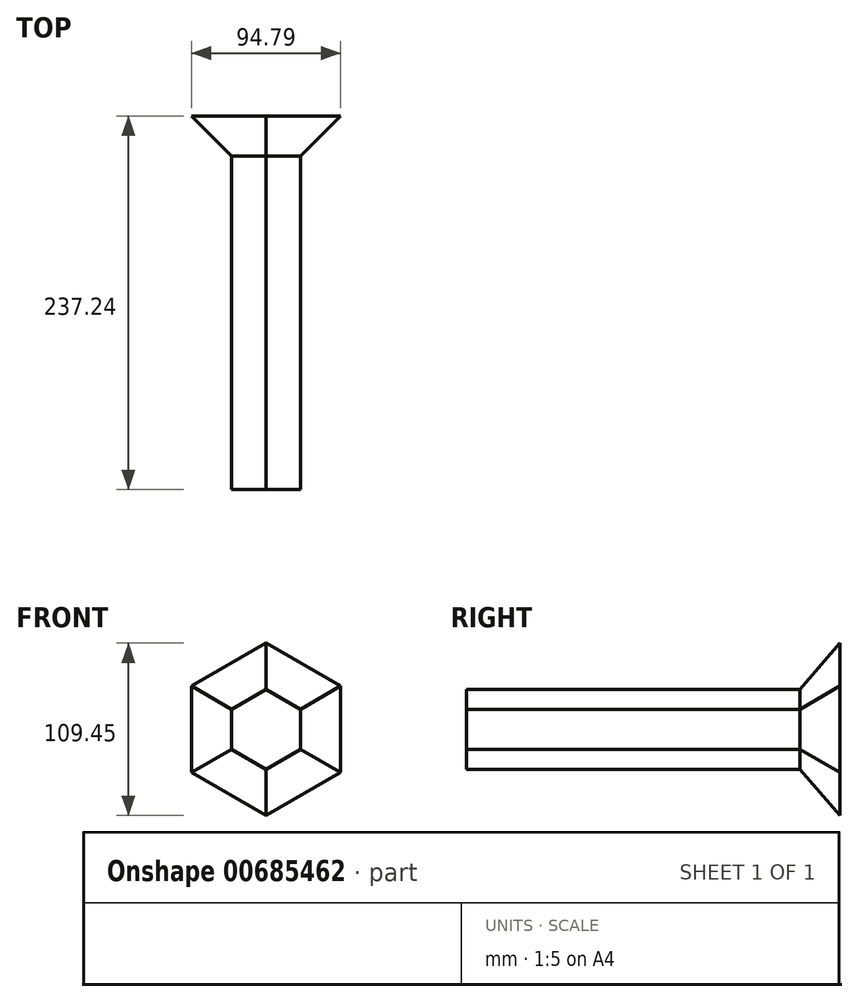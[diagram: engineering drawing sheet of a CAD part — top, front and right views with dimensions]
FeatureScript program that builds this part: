
annotation { "Feature Type Name" : "Feature", "Feature Type Description" : "" }
export const myFeature = defineFeature(function(context is Context, id is Id, definition is map)
    precondition{}
    {
        {
            var Q0;
            Q0=qCreatedBy(makeId("Front.planeOp"),FACE);
            var sketch = newSketch(context, id + "F0", { "sketchPlane" : qUnion([Q0])});
            skPoint(sketch, "E0.0.midPoint", {"position": v(16.7, -5.43) * mm});
            skLineSegment(sketch, "E1.0", {"start": v(19.21, 13.6) * mm, "end": v(19.21, -11.8) * mm});
            skLineSegment(sketch, "E1.1", {"start": v(19.21, -11.8) * mm, "end": v(-2.78, -24.5) * mm});
            skLineSegment(sketch, "E1.2", {"start": v(-2.78, -24.5) * mm, "end": v(-24.78, -11.8) * mm});
            skLineSegment(sketch, "E1.3", {"start": v(-24.78, -11.8) * mm, "end": v(-24.78, 13.6) * mm});
            skLineSegment(sketch, "E1.4", {"start": v(-24.78, 13.6) * mm, "end": v(-2.78, 26.3) * mm});
            skLineSegment(sketch, "E1.5", {"start": v(-2.78, 26.3) * mm, "end": v(19.21, 13.6) * mm});
            skSolve(sketch);
        }
        {
            var Q0;
            Q0=makeQuery(id+"F0.imprint","IMPRINT",FACE,{"disambiguationData":[TD([[makeQuery(id+"F0.imprint","IMPRINT",EDGE,{"derivedFrom":sQuery(id+"F0.wireOp",EDGE,"E1.0")}),-1.0]])]});
            extrude(context, id + "F1", {"entities" : qUnion([Q0]), "depth" : 211.84 * mm, "offsetDistance" : 25.4 * mm});
        }
        {
            var Q0;
            Q0=makeQuery(id+"F1.opExtrude","CAP_FACE",FACE,{"disambiguationData":[OSD([sQuery(id+"F0.wireOp",EDGE,"E1.0"),sQuery(id+"F0.wireOp",EDGE,"E1.1"),sQuery(id+"F0.wireOp",EDGE,"E1.2"),sQuery(id+"F0.wireOp",EDGE,"E1.3"),sQuery(id+"F0.wireOp",EDGE,"E1.4"),sQuery(id+"F0.wireOp",EDGE,"E1.5")])],"isStart":true});
            extrude(context, id + "F2", {"entities" : qUnion([Q0]), "operationType" : NewBodyOperationType.ADD, "depth" : 25.4 * mm, "offsetDistance" : 25.4 * mm, "hasDraft" : true, "draftAngle" : 45 * degree});
        }
    });
